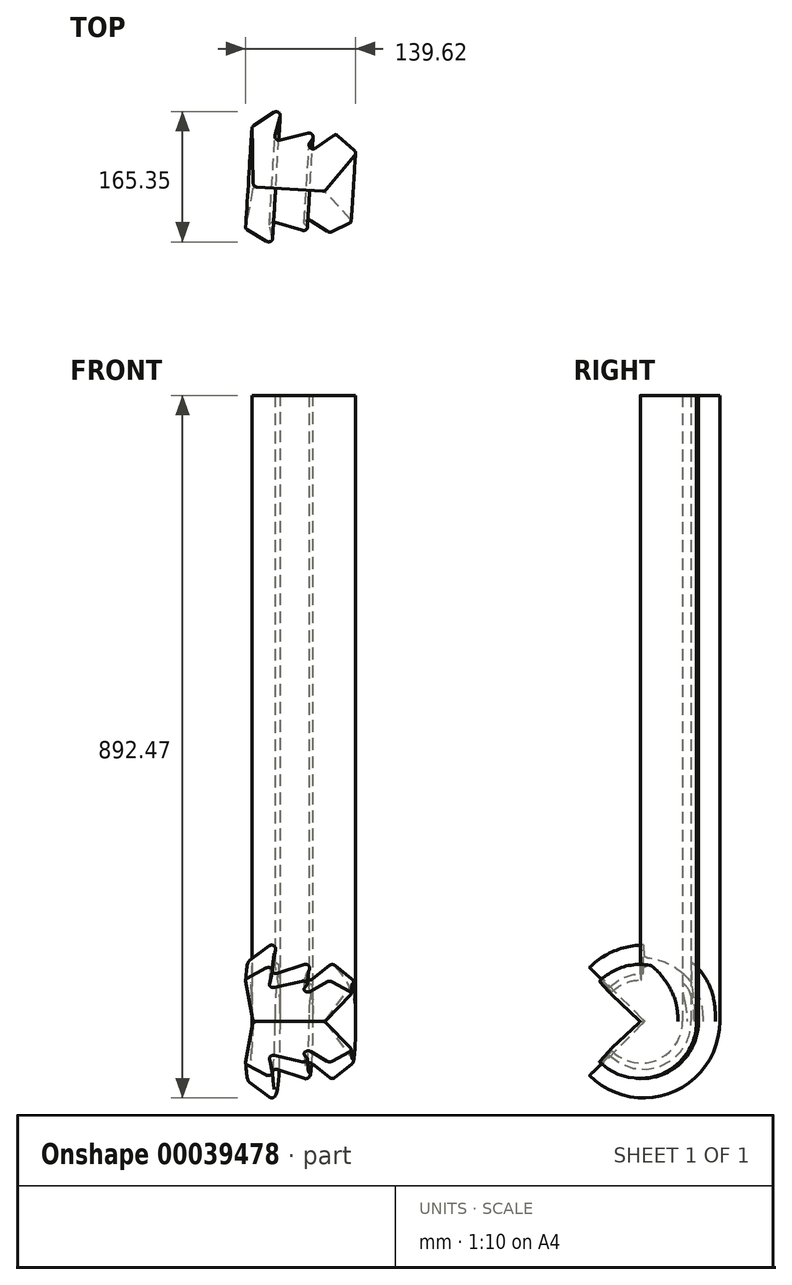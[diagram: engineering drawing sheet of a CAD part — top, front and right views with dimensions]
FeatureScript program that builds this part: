
annotation { "Feature Type Name" : "Feature", "Feature Type Description" : "" }
export const myFeature = defineFeature(function(context is Context, id is Id, definition is map)
    precondition{}
    {
        {
            var Q0;
            Q0=qCreatedBy(makeId("Top.planeOp"),FACE);
            var sketch = newSketch(context, id + "F0", { "sketchPlane" : qUnion([Q0])});
            skLineSegment(sketch, "E0", {"start": v(0, 0) * mm, "end": v(54.63, 38.38) * mm});
            skLineSegment(sketch, "E1", {"start": v(54.63, 38.38) * mm, "end": v(81.57, 14.14) * mm});
            skLineSegment(sketch, "E2", {"start": v(81.57, 14.14) * mm, "end": v(40.4, -34.72) * mm});
            skLineSegment(sketch, "E3", {"start": v(40.4, -34.72) * mm, "end": v(-50.4, -28.95) * mm});
            skLineSegment(sketch, "E4", {"start": v(-50.4, -28.95) * mm, "end": v(-52.13, 47.23) * mm});
            skLineSegment(sketch, "E5", {"start": v(-52.13, 47.23) * mm, "end": v(-12.7, 72.81) * mm});
            skLineSegment(sketch, "E6", {"start": v(-12.7, 72.81) * mm, "end": v(-24.82, 28) * mm});
            skLineSegment(sketch, "E7", {"start": v(-24.82, 28) * mm, "end": v(33.86, 42.8) * mm});
            skLineSegment(sketch, "E8", {"start": v(33.86, 42.8) * mm, "end": v(0, 0) * mm});
            skSolve(sketch);
        }
        {
            var Q0;
            Q0 = qSketchRegion(id + "F0", true);
            extrude(context, id + "F1", {"entities" : qUnion([Q0]), "oppositeDirection" : true, "depth" : 795.43 * mm});
        }
        {
            var Q0;
            Q0=makeQuery(id+"F1.opExtrude","SWEPT_EDGE",EDGE,{"disambiguationData":[OSD([sQuery(id+"F0.wireOp",EDGE,"E6"),sQuery(id+"F0.wireOp",EDGE,"E7")])]});
            var Q1;
            Q1=makeQuery(id+"F1.opExtrude","SWEPT_EDGE",EDGE,{"disambiguationData":[OSD([sQuery(id+"F0.wireOp",EDGE,"E0"),sQuery(id+"F0.wireOp",EDGE,"E8")])]});
            var Q2;
            Q2=makeQuery(id+"F1.opExtrude","SWEPT_EDGE",EDGE,{"disambiguationData":[OSD([sQuery(id+"F0.wireOp",EDGE,"E7"),sQuery(id+"F0.wireOp",EDGE,"E8")])]});
            var Q3;
            Q3=makeQuery(id+"F1.opExtrude","SWEPT_EDGE",EDGE,{"disambiguationData":[OSD([sQuery(id+"F0.wireOp",EDGE,"E0"),sQuery(id+"F0.wireOp",EDGE,"E1")])]});
            var Q4;
            Q4=makeQuery(id+"F1.opExtrude","SWEPT_EDGE",EDGE,{"disambiguationData":[OSD([sQuery(id+"F0.wireOp",EDGE,"E1"),sQuery(id+"F0.wireOp",EDGE,"E2")])]});
            var Q5;
            Q5=makeQuery(id+"F1.opExtrude","SWEPT_EDGE",EDGE,{"disambiguationData":[OSD([sQuery(id+"F0.wireOp",EDGE,"E2"),sQuery(id+"F0.wireOp",EDGE,"E3")])]});
            var Q6;
            Q6=makeQuery(id+"F1.opExtrude","SWEPT_EDGE",EDGE,{"disambiguationData":[OSD([sQuery(id+"F0.wireOp",EDGE,"E3"),sQuery(id+"F0.wireOp",EDGE,"E4")])]});
            var Q7;
            Q7=makeQuery(id+"F1.opExtrude","SWEPT_EDGE",EDGE,{"disambiguationData":[OSD([sQuery(id+"F0.wireOp",EDGE,"E4"),sQuery(id+"F0.wireOp",EDGE,"E5")])]});
            var Q8;
            Q8=makeQuery(id+"F1.opExtrude","SWEPT_EDGE",EDGE,{"disambiguationData":[OSD([sQuery(id+"F0.wireOp",EDGE,"E5"),sQuery(id+"F0.wireOp",EDGE,"E6")])]});
            fillet(context, id + "F2", {"entities" : qUnion([Q0, Q1, Q2, Q3, Q4, Q5, Q6, Q7, Q8]), "radius" : 5.08 * mm, "tangentPropagation" : true, "allowEdgeOverflow" : false});
        }
        {
            var Q0;
            Q0=makeQuery(id+"F1.opExtrude","CAP_FACE",FACE,{"disambiguationData":[OSD([sQuery(id+"F0.wireOp",EDGE,"E0"),sQuery(id+"F0.wireOp",EDGE,"E1"),sQuery(id+"F0.wireOp",EDGE,"E2"),sQuery(id+"F0.wireOp",EDGE,"E3"),sQuery(id+"F0.wireOp",EDGE,"E4"),sQuery(id+"F0.wireOp",EDGE,"E5"),sQuery(id+"F0.wireOp",EDGE,"E6"),sQuery(id+"F0.wireOp",EDGE,"E7"),sQuery(id+"F0.wireOp",EDGE,"E8")])],"isStart":false});
            var Q1;
            Q1=makeQuery(id+"F1.opExtrude","CAP_EDGE",EDGE,{"disambiguationData":[OSD([sQuery(id+"F0.wireOp",EDGE,"E3")])],"isStart":false});
            revolve(context, id + "F3", {"operationType" : NewBodyOperationType.ADD, "entities" : qUnion([Q0]), "axis" : qUnion([Q1]), "revolveType" : RevolveType.SYMMETRIC, "angle" : 270 * degree});
        }
    });
